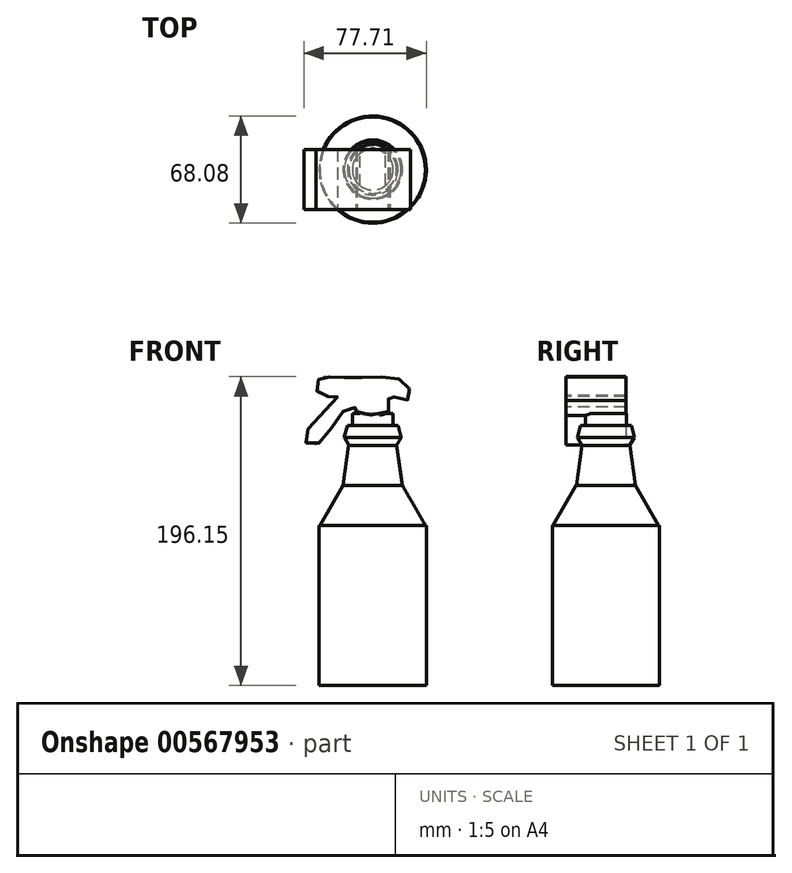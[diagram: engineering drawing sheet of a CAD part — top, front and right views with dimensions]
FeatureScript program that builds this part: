
annotation { "Feature Type Name" : "Feature", "Feature Type Description" : "" }
export const myFeature = defineFeature(function(context is Context, id is Id, definition is map)
    precondition{}
    {
        {
            var Q0;
            Q0=qCreatedBy(makeId("Top.planeOp"),FACE);
            var sketch = newSketch(context, id + "F0", { "sketchPlane" : qUnion([Q0])});
            skCircle(sketch, "E0", {"center": v(0, 0) * mm, "radius": 34.04 * mm});
            skSolve(sketch);
        }
        {
            var Q0;
            Q0 = qSketchRegion(id + "F0", true);
            extrude(context, id + "F1", {"entities" : qUnion([Q0]), "depth" : 101.6 * mm, "offsetDistance" : 25.4 * mm});
        }
        {
            var Q0;
            Q0=makeQuery(id+"F1.opExtrude","CAP_FACE",FACE,{"disambiguationData":[OSD([sQuery(id+"F0.wireOp",EDGE,"E0")])],"isStart":false});
            cPlane(context, id + "F2", {"entities" : qUnion([Q0]), "cplaneType" : CPlaneType.OFFSET, "offset" : 0 * mm, "width" : 152.4 * mm, "height" : 152.4 * mm});
        }
        {
            var Q0;
            Q0=qCreatedBy(id+"F2.planeOp",FACE);
            cPlane(context, id + "F3", {"entities" : qUnion([Q0]), "cplaneType" : CPlaneType.OFFSET, "offset" : 25.4 * mm, "width" : 152.4 * mm, "height" : 152.4 * mm});
        }
        {
            var Q0;
            Q0=qCreatedBy(id+"F2.planeOp",FACE);
            var sketch = newSketch(context, id + "F4", { "sketchPlane" : qUnion([Q0])});
            skCircle(sketch, "E1", {"center": v(0, 0) * mm, "radius": 33.45 * mm});
            skSolve(sketch);
        }
        {
            var Q0;
            Q0=qCreatedBy(id+"F3.planeOp",FACE);
            var sketch = newSketch(context, id + "F5", { "sketchPlane" : qUnion([Q0])});
            skCircle(sketch, "E2", {"center": v(0, 0) * mm, "radius": 18.86 * mm});
            skSolve(sketch);
        }
        {
            var Q1;
            Q1=makeQuery(id+"F4.imprint","IMPRINT",FACE,{"disambiguationData":[TD([[makeQuery(id+"F4.imprint","IMPRINT",EDGE,{"derivedFrom":sQuery(id+"F4.wireOp",EDGE,"E1")}),1.0]])]});
            var Q2;
            Q2=makeQuery(id+"F5.imprint","IMPRINT",FACE,{"disambiguationData":[TD([[makeQuery(id+"F5.imprint","IMPRINT",EDGE,{"derivedFrom":sQuery(id+"F5.wireOp",EDGE,"E2")}),1.0]])]});
            loft(context, id + "F6", {"operationType" : NewBodyOperationType.ADD, "sheetProfilesArray" : [{ "sheetProfileEntities" : qUnion([Q1]) }, { "sheetProfileEntities" : qUnion([Q2]) }]});
        }
        {
            var Q0;
            Q0=qCreatedBy(id+"F3.planeOp",FACE);
            var sketch = newSketch(context, id + "F7", { "sketchPlane" : qUnion([Q0])});
            skCircle(sketch, "E3", {"center": v(0, 0) * mm, "radius": 18.75 * mm});
            skSolve(sketch);
        }
        {
            var Q0;
            Q0=qCreatedBy(id+"F3.planeOp",FACE);
            cPlane(context, id + "F8", {"entities" : qUnion([Q0]), "cplaneType" : CPlaneType.OFFSET, "offset" : 25.4 * mm, "width" : 152.4 * mm, "height" : 152.4 * mm});
        }
        {
            var Q0;
            Q0=qCreatedBy(id+"F8.planeOp",FACE);
            var sketch = newSketch(context, id + "F9", { "sketchPlane" : qUnion([Q0])});
            skCircle(sketch, "E4", {"center": v(0, 0) * mm, "radius": 15.25 * mm});
            skSolve(sketch);
        }
        {
            var Q1;
            Q1=makeQuery(id+"F7.imprint","IMPRINT",FACE,{"disambiguationData":[TD([[makeQuery(id+"F7.imprint","IMPRINT",EDGE,{"derivedFrom":sQuery(id+"F7.wireOp",EDGE,"E3")}),1.0]])]});
            var Q2;
            Q2=makeQuery(id+"F9.imprint","IMPRINT",FACE,{"disambiguationData":[TD([[makeQuery(id+"F9.imprint","IMPRINT",EDGE,{"derivedFrom":sQuery(id+"F9.wireOp",EDGE,"E4")}),1.0]])]});
            loft(context, id + "F10", {"operationType" : NewBodyOperationType.ADD, "sheetProfilesArray" : [{ "sheetProfileEntities" : qUnion([Q1]) }, { "sheetProfileEntities" : qUnion([Q2]) }]});
        }
        {
            var Q0;
            Q0=qCreatedBy(id+"F8.planeOp",FACE);
            var sketch = newSketch(context, id + "F11", { "sketchPlane" : qUnion([Q0])});
            skCircle(sketch, "E5", {"center": v(0, 0) * mm, "radius": 15.1 * mm});
            skSolve(sketch);
        }
        {
            var Q0;
            Q0=qCreatedBy(id+"F8.planeOp",FACE);
            cPlane(context, id + "F12", {"entities" : qUnion([Q0]), "cplaneType" : CPlaneType.OFFSET, "offset" : 5.08 * mm, "width" : 152.4 * mm, "height" : 152.4 * mm});
        }
        {
            var Q0;
            Q0=qCreatedBy(id+"F12.planeOp",FACE);
            var sketch = newSketch(context, id + "F13", { "sketchPlane" : qUnion([Q0])});
            skCircle(sketch, "E6", {"center": v(0, 0) * mm, "radius": 18.05 * mm});
            skSolve(sketch);
        }
        {
            var Q1;
            Q1 = qSketchRegion(id + "F11", true);
            var Q2;
            Q2=makeQuery(id+"F13.imprint","IMPRINT",FACE,{"disambiguationData":[TD([[makeQuery(id+"F13.imprint","IMPRINT",EDGE,{"derivedFrom":sQuery(id+"F13.wireOp",EDGE,"E6")}),1.0]])]});
            loft(context, id + "F14", {"operationType" : NewBodyOperationType.ADD, "sheetProfilesArray" : [{ "sheetProfileEntities" : qUnion([Q1]) }, { "sheetProfileEntities" : qUnion([Q2]) }]});
        }
        {
            var Q0;
            Q0=makeQuery(id+"F14.opLoft","CAP_FACE",FACE,{"disambiguationData":[OSD([makeQuery(id+"F13.imprint","IMPRINT",FACE,{"disambiguationData":[TD([[makeQuery(id+"F13.imprint","IMPRINT",EDGE,{"derivedFrom":sQuery(id+"F13.wireOp",EDGE,"E6")}),1.0]])]})])],"isStart":true});
            var sketch = newSketch(context, id + "F15", { "sketchPlane" : qUnion([Q0])});
            skCircle(sketch, "E7", {"center": v(0, 0) * mm, "radius": 18.1 * mm});
            skSolve(sketch);
        }
        {
            var Q0;
            Q0=qCreatedBy(id+"F12.planeOp",FACE);
            cPlane(context, id + "F16", {"entities" : qUnion([Q0]), "cplaneType" : CPlaneType.OFFSET, "offset" : 7.62 * mm, "width" : 152.4 * mm, "height" : 152.4 * mm});
        }
        {
            var Q0;
            Q0=qCreatedBy(id+"F16.planeOp",FACE);
            var sketch = newSketch(context, id + "F17", { "sketchPlane" : qUnion([Q0])});
            skCircle(sketch, "E8", {"center": v(0, 0) * mm, "radius": 16.11 * mm});
            skSolve(sketch);
        }
        {
            var Q1;
            Q1 = qSketchRegion(id + "F15", true);
            var Q2;
            Q2=makeQuery(id+"F17.imprint","IMPRINT",FACE,{"disambiguationData":[TD([[makeQuery(id+"F17.imprint","IMPRINT",EDGE,{"derivedFrom":sQuery(id+"F17.wireOp",EDGE,"E8")}),1.0]])]});
            loft(context, id + "F18", {"operationType" : NewBodyOperationType.ADD, "sheetProfilesArray" : [{ "sheetProfileEntities" : qUnion([Q1]) }, { "sheetProfileEntities" : qUnion([Q2]) }]});
        }
        {
            var Q0;
            Q0=qCreatedBy(id+"F16.planeOp",FACE);
            var sketch = newSketch(context, id + "F19", { "sketchPlane" : qUnion([Q0])});
            skCircle(sketch, "E9", {"center": v(0, 0) * mm, "radius": 12.98 * mm});
            skSolve(sketch);
        }
        {
            var Q0;
            Q0 = qSketchRegion(id + "F19", true);
            extrude(context, id + "F20", {"entities" : qUnion([Q0]), "operationType" : NewBodyOperationType.ADD, "depth" : 7.62 * mm, "offsetDistance" : 25.4 * mm});
        }
        {
            var Q0;
            Q0=qCreatedBy(makeId("Front.planeOp"),FACE);
            var sketch = newSketch(context, id + "F21", { "sketchPlane" : qUnion([Q0])});
            skFitSpline(sketch, "E10", {"points": [v(10.07, 174.01) * mm, v(10.07, 184.08) * mm, v(21.8, 181.28) * mm, v(21.8, 191.35) * mm, v(0, 195.82) * mm, v(-24.04, 195.82) * mm, v(-34.67, 194.15) * mm, v(-33, 184.08) * mm, v(-22.37, 183.52) * mm, v(-43.62, 157.8) * mm, v(-35.23, 153.33) * mm, v(-16.78, 175.7) * mm, v(-10.07, 175.7) * mm, v(-10.62, 174.01) * mm, v(10.07, 174.01) * mm]});
            skSolve(sketch);
        }
        {
            var Q0;
            Q0 = qSketchRegion(id + "F21", true);
            extrude(context, id + "F22", {"entities" : qUnion([Q0]), "operationType" : NewBodyOperationType.ADD, "depth" : 25.4 * mm, "offsetDistance" : 25.4 * mm});
        }
        {
            var Q0;
            Q0=makeQuery(id+"F22.opExtrude","CAP_FACE",FACE,{"disambiguationData":[OSD([sQuery(id+"F21.wireOp",EDGE,"E10")])],"isStart":true});
            extrude(context, id + "F23", {"entities" : qUnion([Q0]), "operationType" : NewBodyOperationType.ADD, "depth" : 12.7 * mm, "offsetDistance" : 25.4 * mm});
        }
    });
